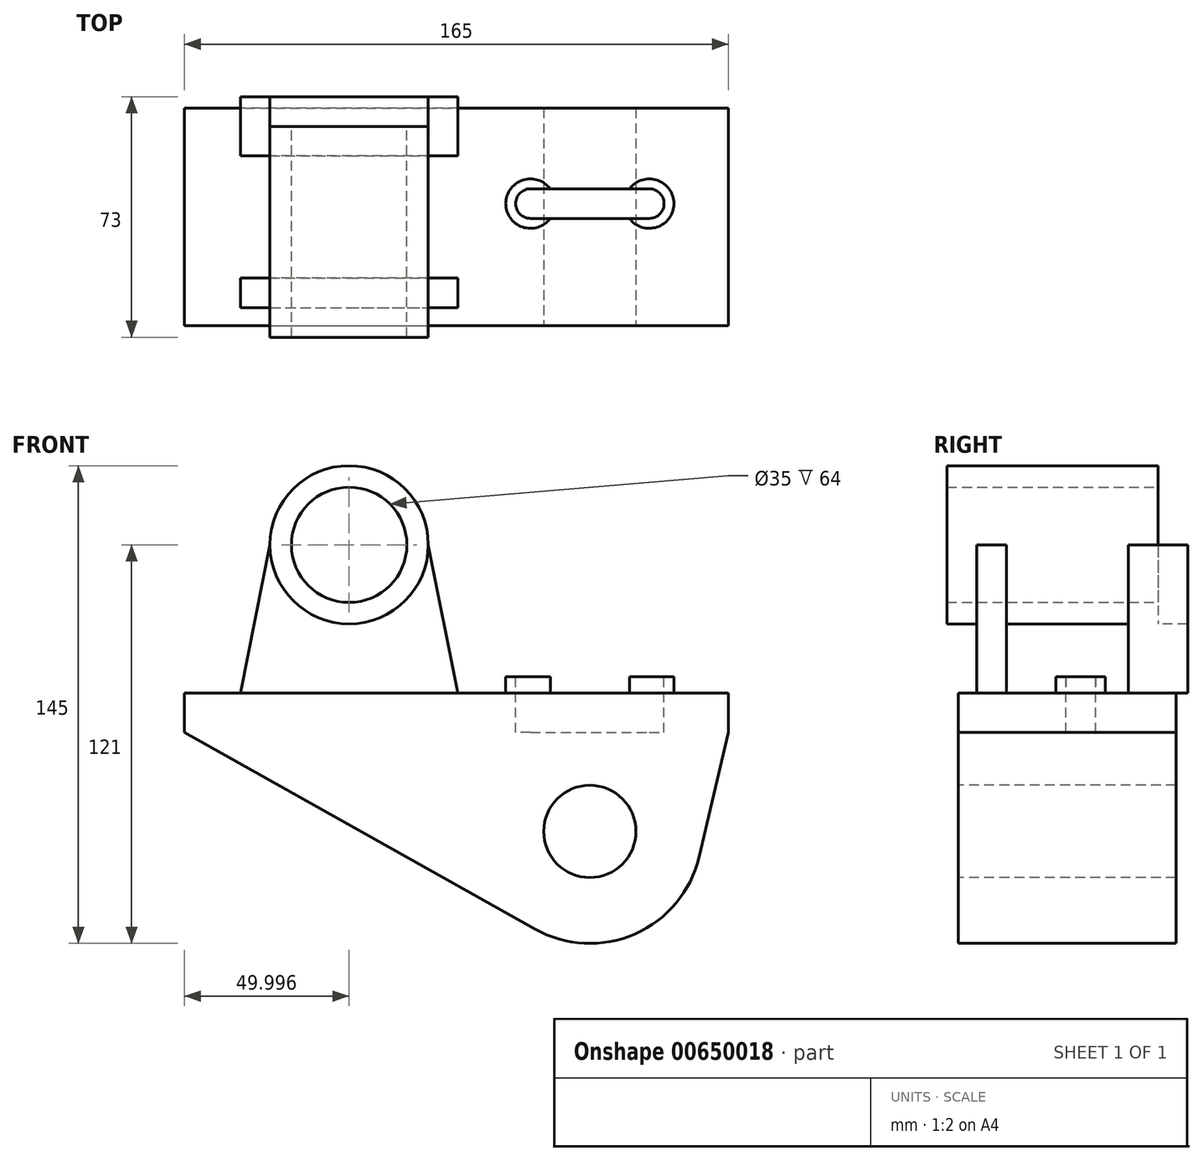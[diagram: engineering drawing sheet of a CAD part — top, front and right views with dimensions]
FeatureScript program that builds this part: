
annotation { "Feature Type Name" : "Feature", "Feature Type Description" : "" }
export const myFeature = defineFeature(function(context is Context, id is Id, definition is map)
    precondition{}
    {
        {
            var Q0;
            Q0=qCreatedBy(makeId("Top.planeOp"),FACE);
            var sketch = newSketch(context, id + "F0", { "sketchPlane" : qUnion([Q0])});
            skLineSegment(sketch, "E0", {"start": v(-33.35, -25.9) * mm, "end": v(131.65, -25.9) * mm});
            skLineSegment(sketch, "E1", {"start": v(131.65, -25.9) * mm, "end": v(131.65, 40.1) * mm});
            skLineSegment(sketch, "E2", {"start": v(131.65, 40.1) * mm, "end": v(-33.35, 40.1) * mm});
            skLineSegment(sketch, "E3", {"start": v(-33.35, 40.1) * mm, "end": v(-33.35, -25.9) * mm});
            skSolve(sketch);
        }
        {
            var Q0;
            Q0 = qSketchRegion(id + "F0", true);
            extrude(context, id + "F1", {"entities" : qUnion([Q0]), "depth" : 12 * mm, "offsetDistance" : 25 * mm});
        }
        {
            var Q0;
            Q0=makeQuery(id+"F1.opExtrude","CAP_FACE",FACE,{"disambiguationData":[OSD([sQuery(id+"F0.wireOp",EDGE,"E0"),sQuery(id+"F0.wireOp",EDGE,"E1"),sQuery(id+"F0.wireOp",EDGE,"E2"),sQuery(id+"F0.wireOp",EDGE,"E3")])],"isStart":false});
            var sketch = newSketch(context, id + "F2", { "sketchPlane" : qUnion([Q0])});
            skLineSegment(sketch, "E4", {"start": v(89.65, -17.8) * mm, "end": v(89.65, 40.1) * mm});
            skLineSegment(sketch, "E5", {"start": v(89.65, -17.8) * mm, "end": v(89.65, -25.9) * mm});
            skLineSegment(sketch, "E6", {"start": v(89.65, 11.15) * mm, "end": v(89.65, 18.65) * mm});
            skLineSegment(sketch, "E7", {"start": v(89.65, 18.65) * mm, "end": v(89.65, 3.65) * mm});
            skLineSegment(sketch, "E8", {"start": v(89.65, 18.65) * mm, "end": v(107.65, 18.65) * mm});
            skLineSegment(sketch, "E9", {"start": v(107.65, 18.65) * mm, "end": v(71.65, 18.65) * mm});
            skLineSegment(sketch, "E10", {"start": v(71.65, 18.65) * mm, "end": v(71.65, 3.65) * mm});
            skLineSegment(sketch, "E11", {"start": v(71.65, 3.65) * mm, "end": v(107.65, 3.65) * mm});
            skLineSegment(sketch, "E12", {"start": v(107.65, 3.65) * mm, "end": v(107.65, 18.65) * mm});
            skPoint(sketch, "E13.center.orphan", {"position": v(71.65, 11.15) * mm});
            skPoint(sketch, "E14.center.orphan", {"position": v(107.65, 11.15) * mm});
            skCircle(sketch, "E15", {"center": v(71.65, 11.15) * mm, "radius": 7.5 * mm});
            skCircle(sketch, "E16", {"center": v(107.65, 11.15) * mm, "radius": 7.5 * mm});
            skSolve(sketch);
        }
        {
            var Q0;
            {var subQ0=sQuery(id+"F2.wireOp",EDGE,"E10");Q0=makeQuery(id+"F2.imprint","IMPRINT",FACE,{"disambiguationData":[TD([[makeQuery(id+"F2.imprint","IMPRINT",EDGE,{"derivedFrom":subQ0}),1.0]])]});}
            var Q1;
            {var subQ0=sQuery(id+"F2.wireOp",EDGE,"E10");Q1=makeQuery(id+"F2.imprint","IMPRINT",FACE,{"disambiguationData":[TD([[makeQuery(id+"F2.imprint","IMPRINT",EDGE,{"derivedFrom":subQ0}),-1.0]])]});}
            var Q2;
            {var subQ1=sQuery(id+"F2.wireOp",EDGE,"E7");var subQ10=makeQuery(id+"F2.imprint","IMPRINT",VERTEX,{"derivedFrom":subQ1});Q2=makeQuery(id+"F2.imprint","IMPRINT",FACE,{"disambiguationData":[TD([[makeQuery(id+"F2.imprint","IMPRINT",EDGE,{"disambiguationData":[TD([[subQ10,1.0]])],"derivedFrom":subQ1}),1.0]])]});}
            var Q3;
            {var subQ0=sQuery(id+"F2.wireOp",EDGE,"E12");Q3=makeQuery(id+"F2.imprint","IMPRINT",FACE,{"disambiguationData":[TD([[makeQuery(id+"F2.imprint","IMPRINT",EDGE,{"derivedFrom":subQ0}),1.0]])]});}
            var Q4;
            {var subQ0=sQuery(id+"F2.wireOp",EDGE,"E12");Q4=makeQuery(id+"F2.imprint","IMPRINT",FACE,{"disambiguationData":[TD([[makeQuery(id+"F2.imprint","IMPRINT",EDGE,{"derivedFrom":subQ0}),-1.0]])]});}
            var Q5;
            {var subQ1=sQuery(id+"F2.wireOp",EDGE,"E7");var subQ9=makeQuery(id+"F2.imprint","IMPRINT",VERTEX,{"derivedFrom":subQ1});Q5=makeQuery(id+"F2.imprint","IMPRINT",FACE,{"disambiguationData":[TD([[makeQuery(id+"F2.imprint","IMPRINT",EDGE,{"disambiguationData":[TD([[subQ9,1.0]])],"derivedFrom":subQ1}),-1.0]])]});}
            extrude(context, id + "F3", {"entities" : qUnion([Q0, Q1, Q2, Q3, Q4, Q5]), "operationType" : NewBodyOperationType.ADD, "depth" : 5 * mm, "offsetDistance" : 25 * mm});
        }
        {
            var Q0;
            Q0=makeQuery(id+"F3.opExtrude","CAP_FACE",FACE,{"disambiguationData":[OSD([sQuery(id+"F2.wireOp",EDGE,"E9"),sQuery(id+"F2.wireOp",EDGE,"E11"),sQuery(id+"F2.wireOp",EDGE,"E15"),sQuery(id+"F2.wireOp",EDGE,"E16")])],"isStart":false});
            var sketch = newSketch(context, id + "F4", { "sketchPlane" : qUnion([Q0])});
            skLineSegment(sketch, "E17", {"start": v(89.65, 3.65) * mm, "end": v(89.65, 6.65) * mm});
            skLineSegment(sketch, "E18", {"start": v(89.65, 18.65) * mm, "end": v(89.65, 15.65) * mm});
            skLineSegment(sketch, "E19", {"start": v(89.65, 15.65) * mm, "end": v(107.65, 15.65) * mm});
            skLineSegment(sketch, "E20", {"start": v(107.65, 15.65) * mm, "end": v(71.65, 15.65) * mm});
            skLineSegment(sketch, "E21", {"start": v(71.65, 15.65) * mm, "end": v(71.65, 6.65) * mm});
            skLineSegment(sketch, "E22", {"start": v(71.65, 6.65) * mm, "end": v(107.65, 6.65) * mm});
            skLineSegment(sketch, "E23", {"start": v(107.65, 6.65) * mm, "end": v(107.65, 15.65) * mm});
            skCircle(sketch, "E24", {"center": v(71.65, 11.15) * mm, "radius": 4.5 * mm});
            skCircle(sketch, "E25", {"center": v(107.65, 11.15) * mm, "radius": 4.5 * mm});
            skSolve(sketch);
        }
        {
            var Q0;
            Q0 = qSketchRegion(id + "F4", true);
            extrude(context, id + "F5", {"entities" : qUnion([Q0]), "operationType" : NewBodyOperationType.REMOVE, "oppositeDirection" : true, "depth" : 25 * mm, "offsetDistance" : 25 * mm});
        }
        {
            var Q0;
            Q0=makeQuery(id+"F1.opExtrude","CAP_FACE",FACE,{"disambiguationData":[OSD([sQuery(id+"F0.wireOp",EDGE,"E0"),sQuery(id+"F0.wireOp",EDGE,"E1"),sQuery(id+"F0.wireOp",EDGE,"E2"),sQuery(id+"F0.wireOp",EDGE,"E3")])],"isStart":false});
            var sketch = newSketch(context, id + "F6", { "sketchPlane" : qUnion([Q0])});
            skLineSegment(sketch, "E26", {"start": v(16.65, -20.4) * mm, "end": v(16.65, 34.6) * mm});
            skLineSegment(sketch, "E27", {"start": v(16.65, 7.1) * mm, "end": v(16.65, 34.6) * mm});
            skLineSegment(sketch, "E28", {"start": v(16.65, 7.1) * mm, "end": v(16.65, -20.4) * mm});
            skLineSegment(sketch, "E29", {"start": v(16.65, -20.4) * mm, "end": v(16.65, -11.4) * mm});
            skLineSegment(sketch, "E30", {"start": v(16.65, 34.6) * mm, "end": v(16.65, 25.6) * mm});
            skLineSegment(sketch, "E31", {"start": v(16.65, -20.4) * mm, "end": v(49.65, -20.4) * mm});
            skLineSegment(sketch, "E32", {"start": v(49.65, -20.4) * mm, "end": v(49.65, -11.4) * mm});
            skLineSegment(sketch, "E33", {"start": v(49.65, -11.4) * mm, "end": v(16.65, -11.4) * mm});
            skLineSegment(sketch, "E34", {"start": v(16.65, -11.4) * mm, "end": v(-16.35, -11.4) * mm});
            skLineSegment(sketch, "E35", {"start": v(-16.35, -11.4) * mm, "end": v(-16.35, -20.4) * mm});
            skLineSegment(sketch, "E36", {"start": v(-16.35, -20.4) * mm, "end": v(16.65, -20.4) * mm});
            skPoint(sketch, "E37.end.orphan", {"position": v(49.65, -25.9) * mm});
            skPoint(sketch, "E38.end.orphan", {"position": v(-16.35, -25.9) * mm});
            skPoint(sketch, "E39.orphan", {"position": v(16.65, -25.9) * mm});
            skPoint(sketch, "E40.orphan", {"position": v(16.65, 40.1) * mm});
            skLineSegment(sketch, "E41", {"start": v(-33.35, 7.1) * mm, "end": v(131.65, 7.1) * mm});
            skLineSegment(sketch, "E42.MirrorCS", {"start": v(49.65, 25.6) * mm, "end": v(16.65, 25.6) * mm});
            skLineSegment(sketch, "E43.MirrorCS", {"start": v(49.65, 34.6) * mm, "end": v(49.65, 25.6) * mm});
            skLineSegment(sketch, "E44.MirrorCS", {"start": v(16.65, 34.6) * mm, "end": v(49.65, 34.6) * mm});
            skLineSegment(sketch, "E45.MirrorCS", {"start": v(16.65, 25.6) * mm, "end": v(-16.35, 25.6) * mm});
            skLineSegment(sketch, "E46.MirrorCS", {"start": v(-16.35, 34.6) * mm, "end": v(16.65, 34.6) * mm});
            skLineSegment(sketch, "E47.MirrorCS", {"start": v(-16.35, 25.6) * mm, "end": v(-16.35, 34.6) * mm});
            skSolve(sketch);
        }
        {
            var Q0;
            Q0 = qSketchRegion(id + "F6", true);
            extrude(context, id + "F7", {"entities" : qUnion([Q0]), "operationType" : NewBodyOperationType.ADD, "depth" : 45 * mm, "offsetDistance" : 25 * mm});
        }
        {
            var Q0;
            Q0=makeQuery(id+"F7.opExtrude","SWEPT_FACE",FACE,{"disambiguationData":[OSD([sQuery(id+"F6.wireOp",EDGE,"E31"),sQuery(id+"F6.wireOp",EDGE,"E36")])]});
            var sketch = newSketch(context, id + "F8", { "sketchPlane" : qUnion([Q0])});
            skCircle(sketch, "E48", {"center": v(16.65, 57) * mm, "radius": 24 * mm});
            skCircle(sketch, "E49", {"center": v(16.65, 57) * mm, "radius": 10 * mm});
            skSolve(sketch);
        }
        {
            var Q0;
            {var subQ0=sQuery(id+"F8.wireOp",EDGE,"E48");var subQ1=makeQuery(id+"F7.opExtrude","CAP_EDGE",EDGE,{"disambiguationData":[OSD([sQuery(id+"F6.wireOp",EDGE,"E31"),sQuery(id+"F6.wireOp",EDGE,"E36")])],"isStart":false});var subQ2=makeQuery(id+"F8.imprint","INTERSECT",VERTEX,{"disambiguationData":[OD(0.0)],"derivedFrom":[subQ1,subQ0]});Q0=makeQuery(id+"F8.imprint","IMPRINT",FACE,{"disambiguationData":[TD([[makeQuery(id+"F8.imprint","IMPRINT",EDGE,{"disambiguationData":[TD([[subQ2,-1.0]])],"derivedFrom":subQ0}),1.0]])]});}
            var Q1;
            {var subQ0=sQuery(id+"F8.wireOp",EDGE,"E48");var subQ1=makeQuery(id+"F7.opExtrude","CAP_EDGE",EDGE,{"disambiguationData":[OSD([sQuery(id+"F6.wireOp",EDGE,"E31"),sQuery(id+"F6.wireOp",EDGE,"E36")])],"isStart":false});var subQ2=makeQuery(id+"F8.imprint","INTERSECT",VERTEX,{"disambiguationData":[OD(0.0)],"derivedFrom":[subQ1,subQ0]});Q1=makeQuery(id+"F8.imprint","IMPRINT",FACE,{"disambiguationData":[TD([[makeQuery(id+"F8.imprint","IMPRINT",EDGE,{"disambiguationData":[TD([[subQ2,1.0]])],"derivedFrom":subQ0}),1.0]])]});}
            extrude(context, id + "F9", {"entities" : qUnion([Q0, Q1]), "operationType" : NewBodyOperationType.ADD, "oppositeDirection" : true, "depth" : 55 * mm, "offsetDistance" : 25 * mm});
        }
        {
            var Q0;
            {var subQ0=sQuery(id+"F8.wireOp",EDGE,"E49");var subQ1=makeQuery(id+"F7.opExtrude","CAP_EDGE",EDGE,{"disambiguationData":[OSD([sQuery(id+"F6.wireOp",EDGE,"E31"),sQuery(id+"F6.wireOp",EDGE,"E36")])],"isStart":false});var subQ2=makeQuery(id+"F8.imprint","INTERSECT",VERTEX,{"disambiguationData":[OD(0.0)],"derivedFrom":[subQ1,subQ0]});Q0=makeQuery(id+"F8.imprint","IMPRINT",FACE,{"disambiguationData":[TD([[makeQuery(id+"F8.imprint","IMPRINT",EDGE,{"disambiguationData":[TD([[subQ2,1.0]])],"derivedFrom":subQ0}),1.0]])]});}
            extrude(context, id + "F10", {"entities" : qUnion([Q0]), "operationType" : NewBodyOperationType.REMOVE, "oppositeDirection" : true, "depth" : 115.6 * mm, "offsetDistance" : 25 * mm});
        }
        {
            var Q0;
            Q0=makeQuery(id+"F9.boolean.opBoolean","MERGE",FACE,{"derivedFrom":[makeQuery(id+"F7.opExtrude","SWEPT_FACE",FACE,{"disambiguationData":[OSD([sQuery(id+"F6.wireOp",EDGE,"E44.MirrorCS"),sQuery(id+"F6.wireOp",EDGE,"E46.MirrorCS")])]}),makeQuery(id+"F9.opExtrude","CAP_FACE",FACE,{"disambiguationData":[OSD([sQuery(id+"F8.wireOp",EDGE,"E48"),sQuery(id+"F8.wireOp",EDGE,"E49")])],"isStart":false})]});
            var sketch = newSketch(context, id + "F11", { "sketchPlane" : qUnion([Q0])});
            skCircle(sketch, "E50", {"center": v(-16.65, 57) * mm, "radius": 17.5 * mm});
            skSolve(sketch);
        }
        {
            var Q0;
            Q0=makeQuery(id+"F11.imprint","IMPRINT",FACE,{"disambiguationData":[TD([[makeQuery(id+"F11.imprint","IMPRINT",EDGE,{"derivedFrom":sQuery(id+"F11.wireOp",EDGE,"E50")}),1.0]])]});
            extrude(context, id + "F12", {"entities" : qUnion([Q0]), "operationType" : NewBodyOperationType.REMOVE, "oppositeDirection" : true, "depth" : 433.7 * mm, "offsetDistance" : 25 * mm});
        }
        {
            var Q0;
            {var subQ0=sQuery(id+"F8.wireOp",EDGE,"E48");var subQ1=makeQuery(id+"F7.opExtrude","CAP_EDGE",EDGE,{"disambiguationData":[OSD([sQuery(id+"F6.wireOp",EDGE,"E31"),sQuery(id+"F6.wireOp",EDGE,"E36")])],"isStart":false});var subQ2=makeQuery(id+"F8.imprint","INTERSECT",VERTEX,{"disambiguationData":[OD(0.0)],"derivedFrom":[subQ1,subQ0]});Q0=makeQuery(id+"F8.imprint","IMPRINT",FACE,{"disambiguationData":[TD([[makeQuery(id+"F8.imprint","IMPRINT",EDGE,{"disambiguationData":[TD([[subQ2,1.0]])],"derivedFrom":subQ0}),1.0]])]});}
            var Q1;
            {var subQ0=sQuery(id+"F8.wireOp",EDGE,"E48");var subQ1=makeQuery(id+"F7.opExtrude","CAP_EDGE",EDGE,{"disambiguationData":[OSD([sQuery(id+"F6.wireOp",EDGE,"E31"),sQuery(id+"F6.wireOp",EDGE,"E36")])],"isStart":false});var subQ2=makeQuery(id+"F8.imprint","INTERSECT",VERTEX,{"disambiguationData":[OD(0.0)],"derivedFrom":[subQ1,subQ0]});Q1=makeQuery(id+"F8.imprint","IMPRINT",FACE,{"disambiguationData":[TD([[makeQuery(id+"F8.imprint","IMPRINT",EDGE,{"disambiguationData":[TD([[subQ2,-1.0]])],"derivedFrom":subQ0}),1.0]])]});}
            extrude(context, id + "F13", {"entities" : qUnion([Q0, Q1]), "operationType" : NewBodyOperationType.ADD, "depth" : 9 * mm, "offsetDistance" : 25 * mm});
        }
        {
            var Q0;
            Q0=makeQuery(id+"F11.imprint","IMPRINT",FACE,{"disambiguationData":[TD([[makeQuery(id+"F11.imprint","IMPRINT",EDGE,{"derivedFrom":sQuery(id+"F11.wireOp",EDGE,"E50")}),-1.0]])]});
            var sketch = newSketch(context, id + "F14", { "sketchPlane" : qUnion([Q0])});
            skLineSegment(sketch, "E51.0.0", {"start": v(16.35, 12) * mm, "end": v(16.35, 57) * mm});
            skLineSegment(sketch, "E51.0.1", {"start": v(16.35, 57) * mm, "end": v(7.35, 57) * mm});
            skArc(sketch, "E51.0.2", {"start": v(7.35, 57) * mm, "mid": v(-16.65, 81) * mm, "end": v(-40.65, 57) * mm});
            skLineSegment(sketch, "E51.0.3", {"start": v(-40.65, 57) * mm, "end": v(-49.65, 57) * mm});
            skLineSegment(sketch, "E51.0.4", {"start": v(-49.65, 57) * mm, "end": v(-49.65, 12) * mm});
            skLineSegment(sketch, "E51.0.5", {"start": v(-49.65, 12) * mm, "end": v(16.35, 12) * mm});
            skCircle(sketch, "E52", {"center": v(-16.65, 57) * mm, "radius": 24 * mm});
            skSolve(sketch);
        }
        {
            var Q0;
            {var subQ0=sQuery(id+"F14.wireOp",EDGE,"E52");Q0=makeQuery(id+"F14.imprint","IMPRINT",FACE,{"disambiguationData":[TD([[makeQuery(id+"F14.imprint","IMPRINT",EDGE,{"disambiguationData":[OD(0.0)],"derivedFrom":subQ0}),-1.0]])]});}
            extrude(context, id + "F15", {"entities" : qUnion([Q0]), "operationType" : NewBodyOperationType.ADD, "depth" : 9 * mm, "offsetDistance" : 25 * mm});
        }
        {
            var Q0;
            {var subQ2=sQuery(id+"F6.wireOp",EDGE,"E31");var subQ3=makeQuery(id+"F7.opExtrude","SWEPT_EDGE",EDGE,{"disambiguationData":[OSD([subQ2,sQuery(id+"F6.wireOp",EDGE,"E32")])]});Q0=makeQuery(id+"F8.imprint","IMPRINT",FACE,{"disambiguationData":[TD([[makeQuery(id+"F8.imprint","IMPRINT",EDGE,{"derivedFrom":subQ3}),-1.0]])]});}
            var sketch = newSketch(context, id + "F16", { "sketchPlane" : qUnion([Q0])});
            skArc(sketch, "E53.0.0", {"start": v(40.65, 57) * mm, "mid": v(16.65, 33) * mm, "end": v(-7.35, 57) * mm});
            skLineSegment(sketch, "E53.0.1", {"start": v(-7.35, 57) * mm, "end": v(-16.35, 57) * mm});
            skLineSegment(sketch, "E53.0.2", {"start": v(-16.35, 57) * mm, "end": v(-16.35, 12) * mm});
            skLineSegment(sketch, "E53.0.3", {"start": v(-16.35, 12) * mm, "end": v(49.65, 12) * mm});
            skLineSegment(sketch, "E53.0.4", {"start": v(49.65, 12) * mm, "end": v(49.65, 57) * mm});
            skLineSegment(sketch, "E53.0.5", {"start": v(49.65, 57) * mm, "end": v(40.65, 57) * mm});
            skLineSegment(sketch, "E54", {"start": v(-7.35, 57) * mm, "end": v(-16.35, 12) * mm});
            skLineSegment(sketch, "E55", {"start": v(40.65, 57) * mm, "end": v(49.65, 12) * mm});
            skSolve(sketch);
        }
        {
            var Q0;
            Q0=makeQuery(id+"F16.imprint","IMPRINT",FACE,{"disambiguationData":[TD([[makeQuery(id+"F16.imprint","IMPRINT",EDGE,{"derivedFrom":sQuery(id+"F16.wireOp",EDGE,"E53.0.1")}),-1.0]])]});
            var Q1;
            Q1=makeQuery(id+"F16.imprint","IMPRINT",FACE,{"disambiguationData":[TD([[makeQuery(id+"F16.imprint","IMPRINT",EDGE,{"derivedFrom":sQuery(id+"F16.wireOp",EDGE,"E53.0.4")}),-1.0]])]});
            extrude(context, id + "F17", {"entities" : qUnion([Q0, Q1]), "operationType" : NewBodyOperationType.REMOVE, "oppositeDirection" : true, "depth" : 176.2 * mm, "offsetDistance" : 25 * mm});
        }
        {
            var Q0;
            Q0=makeQuery(id+"F11.imprint","IMPRINT",FACE,{"disambiguationData":[TD([[makeQuery(id+"F11.imprint","IMPRINT",EDGE,{"derivedFrom":sQuery(id+"F11.wireOp",EDGE,"E50")}),1.0]])]});
            var sketch = newSketch(context, id + "F18", { "sketchPlane" : qUnion([Q0])});
            skSolve(sketch);
        }
        {
            var Q0;
            Q0=makeQuery(id+"F18.imprint","IMPRINT",FACE,{"disambiguationData":[TD([[makeQuery(id+"F18.imprint","IMPRINT",EDGE,{"derivedFrom":makeQuery(id+"F11.imprint","IMPRINT",EDGE,{"derivedFrom":sQuery(id+"F11.wireOp",EDGE,"E50")})}),1.0]])]});
            extrude(context, id + "F19", {"entities" : qUnion([Q0]), "operationType" : NewBodyOperationType.REMOVE, "oppositeDirection" : true, "depth" : 135.5 * mm, "offsetDistance" : 25 * mm});
        }
        {
            var Q0;
            Q0=makeQuery(id+"F1.opExtrude","CAP_FACE",FACE,{"disambiguationData":[OSD([sQuery(id+"F0.wireOp",EDGE,"E0"),sQuery(id+"F0.wireOp",EDGE,"E1"),sQuery(id+"F0.wireOp",EDGE,"E2"),sQuery(id+"F0.wireOp",EDGE,"E3")])],"isStart":false});
            var sketch = newSketch(context, id + "F20", { "sketchPlane" : qUnion([Q0])});
            skLineSegment(sketch, "E56.0", {"start": v(71.65, 6.65) * mm, "end": v(107.65, 6.65) * mm});
            skLineSegment(sketch, "E57.0.0", {"start": v(131.65, 40.1) * mm, "end": v(-33.35, 40.1) * mm});
            skLineSegment(sketch, "E57.0.1", {"start": v(-33.35, 40.1) * mm, "end": v(-33.35, -25.9) * mm});
            skLineSegment(sketch, "E57.0.2", {"start": v(-33.35, -25.9) * mm, "end": v(131.65, -25.9) * mm});
            skLineSegment(sketch, "E57.0.3", {"start": v(131.65, -25.9) * mm, "end": v(131.65, 40.1) * mm});
            skLineSegment(sketch, "E58.0.2", {"start": v(131.65, -25.9) * mm, "end": v(-33.35, -25.9) * mm});
            skLineSegment(sketch, "E59.0", {"start": v(71.65, 3.65) * mm, "end": v(107.65, 3.65) * mm});
            skLineSegment(sketch, "E60.0", {"start": v(107.65, 15.65) * mm, "end": v(71.65, 15.65) * mm});
            skLineSegment(sketch, "E61", {"start": v(89.65, 15.65) * mm, "end": v(89.65, 6.65) * mm});
            skLineSegment(sketch, "E62", {"start": v(89.65, 6.65) * mm, "end": v(89.65, 11.15) * mm});
            skLineSegment(sketch, "E63", {"start": v(89.65, 11.15) * mm, "end": v(89.65, -25.9) * mm});
            skSolve(sketch);
        }
        {
            var Q0;
            Q0=makeQuery(id+"F1.opExtrude","SWEPT_FACE",FACE,{"disambiguationData":[OSD([sQuery(id+"F0.wireOp",EDGE,"E0")])]});
            var sketch = newSketch(context, id + "F21", { "sketchPlane" : qUnion([Q0])});
            skLineSegment(sketch, "E64.0.0", {"start": v(-33.35, 0) * mm, "end": v(131.65, 0) * mm});
            skLineSegment(sketch, "E64.0.1", {"start": v(131.65, 0) * mm, "end": v(131.65, 12) * mm});
            skLineSegment(sketch, "E64.0.2", {"start": v(131.65, 12) * mm, "end": v(-33.35, 12) * mm});
            skLineSegment(sketch, "E64.0.3", {"start": v(-33.35, 12) * mm, "end": v(-33.35, 0) * mm});
            skPoint(sketch, "E65.0", {"position": v(89.65, 12) * mm});
            skLineSegment(sketch, "E66", {"start": v(89.65, 12) * mm, "end": v(89.65, -30) * mm});
            skCircle(sketch, "E67", {"center": v(89.65, -30) * mm, "radius": 14 * mm});
            skArc(sketch, "E68", {"start": v(73.65, 0) * mm, "mid": v(68.9, -56.94) * mm, "end": v(122.74, -37.8) * mm});
            skLineSegment(sketch, "E69", {"start": v(131.65, 0) * mm, "end": v(122.74, -37.8) * mm});
            skLineSegment(sketch, "E70", {"start": v(-33.35, 0) * mm, "end": v(73.01, -59.65) * mm});
            skSolve(sketch);
        }
        {
            var Q0;
            Q0=makeQuery(id+"F21.imprint","IMPRINT",FACE,{"disambiguationData":[TD([[makeQuery(id+"F21.imprint","IMPRINT",EDGE,{"derivedFrom":sQuery(id+"F21.wireOp",EDGE,"E67")}),-1.0]])]});
            var Q1;
            {var subQ0=sQuery(id+"F21.wireOp",EDGE,"E70");Q1=makeQuery(id+"F21.imprint","IMPRINT",FACE,{"disambiguationData":[TD([[makeQuery(id+"F21.imprint","IMPRINT",EDGE,{"derivedFrom":subQ0}),1.0]])]});}
            extrude(context, id + "F22", {"entities" : qUnion([Q0, Q1]), "operationType" : NewBodyOperationType.ADD, "oppositeDirection" : true, "depth" : 66 * mm, "offsetDistance" : 25 * mm});
        }
    });
